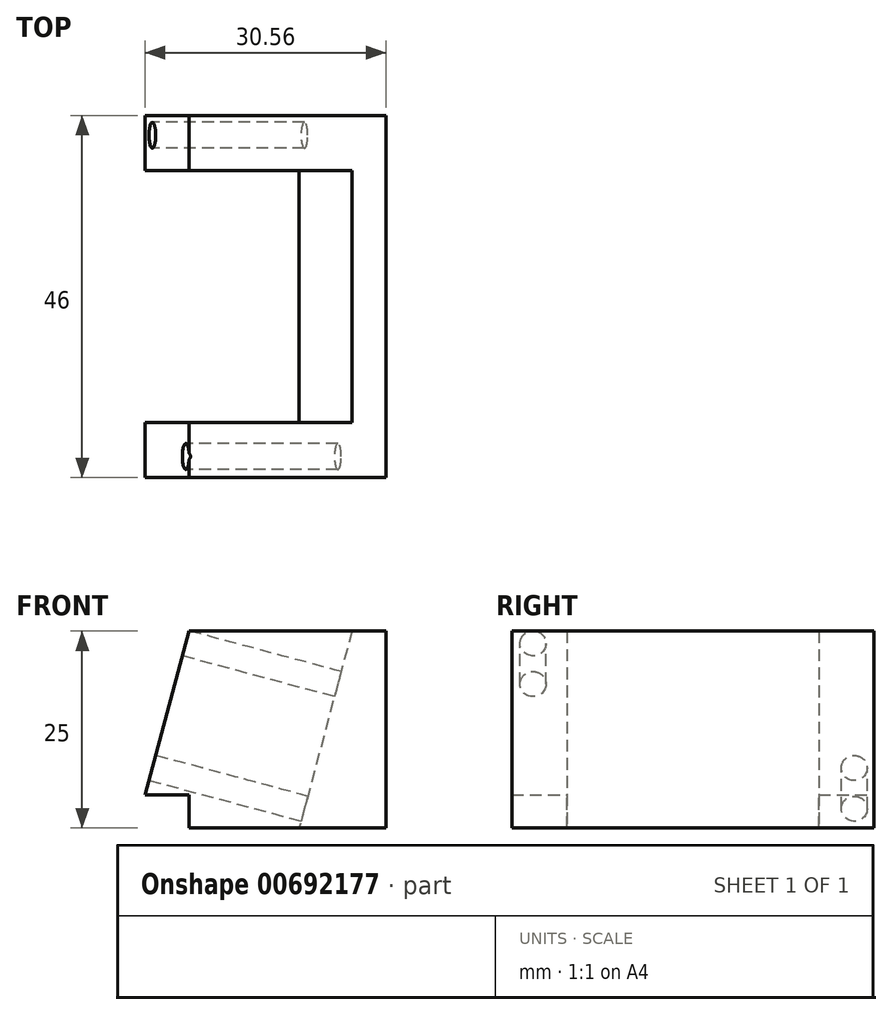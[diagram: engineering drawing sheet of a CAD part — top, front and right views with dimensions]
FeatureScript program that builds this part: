
annotation { "Feature Type Name" : "Feature", "Feature Type Description" : "" }
export const myFeature = defineFeature(function(context is Context, id is Id, definition is map)
    precondition{}
    {
        {
            var Q0;
            Q0=qCreatedBy(makeId("Front.planeOp"),FACE);
            var sketch = newSketch(context, id + "F0", { "sketchPlane" : qUnion([Q0])});
            skLineSegment(sketch, "E0", {"start": v(0, 0) * mm, "end": v(0, 20.77) * mm});
            skLineSegment(sketch, "E1", {"start": v(0, 20.77) * mm, "end": v(-5.56, 0) * mm});
            skLineSegment(sketch, "E2", {"start": v(-5.56, 0) * mm, "end": v(0, 0) * mm});
            skSolve(sketch);
        }
        {
            var Q0;
            Q0=makeQuery(id+"F0.imprint","IMPRINT",FACE,{"disambiguationData":[TD([[makeQuery(id+"F0.imprint","IMPRINT",EDGE,{"derivedFrom":sQuery(id+"F0.wireOp",EDGE,"E0")}),1.0]])]});
            extrude(context, id + "F1", {"entities" : qUnion([Q0]), "depth" : 46 * mm, "offsetDistance" : 25 * mm});
        }
        {
            var Q0;
            Q0=makeQuery(id+"F1.opExtrude","SWEPT_FACE",FACE,{"disambiguationData":[OSD([sQuery(id+"F0.wireOp",EDGE,"E1")])]});
            var sketch = newSketch(context, id + "F2", { "sketchPlane" : qUnion([Q0])});
            skCircle(sketch, "E3", {"center": v(2.5, 2.06) * mm, "radius": 1.65 * mm});
            skCircle(sketch, "E4", {"center": v(43.3, 18.46) * mm, "radius": 1.65 * mm});
            skSolve(sketch);
        }
        {
            var Q0;
            Q0=makeQuery(id+"F1.opExtrude","SWEPT_FACE",FACE,{"disambiguationData":[OSD([sQuery(id+"F0.wireOp",EDGE,"E0")])]});
            var sketch = newSketch(context, id + "F3", { "sketchPlane" : qUnion([Q0])});
            skLineSegment(sketch, "E5.bottom", {"start": v(0, 20.77) * mm, "end": v(-46, 20.77) * mm});
            skLineSegment(sketch, "E5.top", {"start": v(0, -4.23) * mm, "end": v(-46, -4.23) * mm});
            skLineSegment(sketch, "E5.left", {"start": v(0, 20.77) * mm, "end": v(0, -4.23) * mm});
            skLineSegment(sketch, "E5.right", {"start": v(-46, 20.77) * mm, "end": v(-46, -4.23) * mm});
            skSolve(sketch);
        }
        {
            var Q0;
            Q0=makeQuery(id+"F1.opExtrude","SWEPT_FACE",FACE,{"disambiguationData":[OSD([sQuery(id+"F0.wireOp",EDGE,"E1")])]});
            var sketch = newSketch(context, id + "F4", { "sketchPlane" : qUnion([Q0])});
            skLineSegment(sketch, "E6.bottom", {"start": v(7, 33.33) * mm, "end": v(39, 33.33) * mm});
            skLineSegment(sketch, "E6.top", {"start": v(7, -11.67) * mm, "end": v(39, -11.67) * mm});
            skLineSegment(sketch, "E6.left", {"start": v(7, 33.33) * mm, "end": v(7, -11.67) * mm});
            skLineSegment(sketch, "E6.right", {"start": v(39, 33.33) * mm, "end": v(39, -11.67) * mm});
            skSolve(sketch);
        }
        {
            var Q0;
            Q0 = qSketchRegion(id + "F3", true);
            extrude(context, id + "F5", {"entities" : qUnion([Q0]), "operationType" : NewBodyOperationType.ADD, "depth" : 25 * mm, "offsetDistance" : 25 * mm});
        }
        {
            var Q0;
            Q0 = qSketchRegion(id + "F4", true);
            extrude(context, id + "F6", {"entities" : qUnion([Q0]), "operationType" : NewBodyOperationType.REMOVE, "oppositeDirection" : true, "depth" : 20 * mm, "offsetDistance" : 25 * mm});
        }
        {
            var Q0;
            Q0 = qSketchRegion(id + "F2", true);
            extrude(context, id + "F7", {"entities" : qUnion([Q0]), "operationType" : NewBodyOperationType.REMOVE, "oppositeDirection" : true, "depth" : 20 * mm, "offsetDistance" : 25 * mm});
        }
    });
